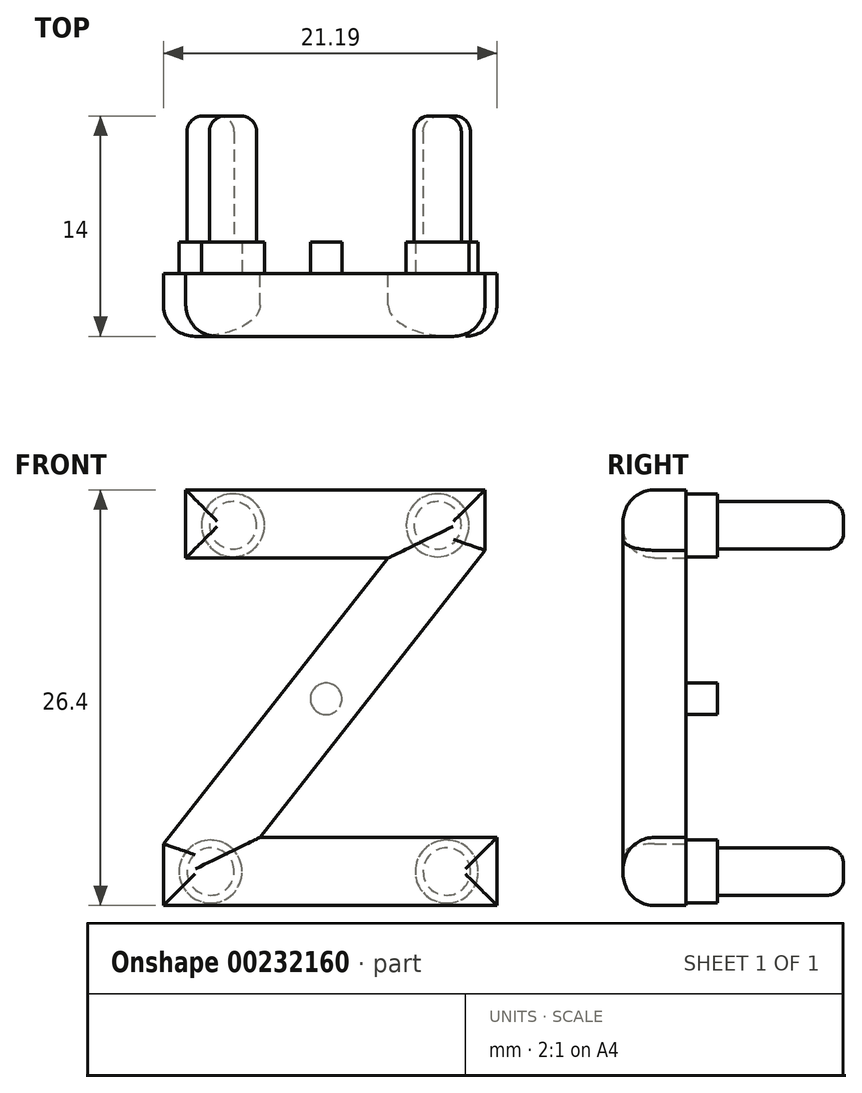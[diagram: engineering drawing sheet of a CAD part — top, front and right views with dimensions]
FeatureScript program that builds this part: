
annotation { "Feature Type Name" : "Feature", "Feature Type Description" : "" }
export const myFeature = defineFeature(function(context is Context, id is Id, definition is map)
    precondition{}
    {
        {
            var Q0;
            Q0=qCreatedBy(makeId("Front.planeOp"),FACE);
            var sketch = newSketch(context, id + "F0", { "sketchPlane" : qUnion([Q0])});
            skText(sketch, "E0", { "text": "Z", "fontName": "Arimo-Bold.ttf"});
            const initialGuessF0  = {"E0": [-0.01481, -0.01752, 1, 0, 0.02763]};
            skSetInitialGuess(sketch, initialGuessF0);
            skSolve(sketch);
        }
        {
            var Q0;
            Q0 = qSketchRegion(id + "F0", true);
            extrude(context, id + "F1", {"entities" : qUnion([Q0]), "depth" : 4 * mm});
        }
        {
            var Q0;
            Q0=makeQuery(id+"F1.opExtrude","CAP_EDGE",EDGE,{"disambiguationData":[OSD([sQuery(id+"F0.wireOp",EDGE,"E0.sketch_text.stroke-4")])],"isStart":false});
            var Q1;
            Q1=makeQuery(id+"F1.opExtrude","CAP_EDGE",EDGE,{"disambiguationData":[OSD([sQuery(id+"F0.wireOp",EDGE,"E0.sketch_text.stroke-5")])],"isStart":false});
            var Q2;
            Q2=makeQuery(id+"F1.opExtrude","CAP_EDGE",EDGE,{"disambiguationData":[OSD([sQuery(id+"F0.wireOp",EDGE,"E0.sketch_text.stroke-3")])],"isStart":false});
            var Q3;
            Q3=makeQuery(id+"F1.opExtrude","CAP_EDGE",EDGE,{"disambiguationData":[OSD([sQuery(id+"F0.wireOp",EDGE,"E0.sketch_text.stroke-6")])],"isStart":false});
            var Q4;
            Q4=makeQuery(id+"F1.opExtrude","CAP_EDGE",EDGE,{"disambiguationData":[OSD([sQuery(id+"F0.wireOp",EDGE,"E0.sketch_text.stroke-7")])],"isStart":false});
            var Q5;
            Q5=makeQuery(id+"F1.opExtrude","CAP_EDGE",EDGE,{"disambiguationData":[OSD([sQuery(id+"F0.wireOp",EDGE,"E0.sketch_text.stroke-2")])],"isStart":false});
            var Q6;
            Q6=makeQuery(id+"F1.opExtrude","CAP_EDGE",EDGE,{"disambiguationData":[OSD([sQuery(id+"F0.wireOp",EDGE,"E0.sketch_text.stroke-1")])],"isStart":false});
            var Q7;
            Q7=makeQuery(id+"F1.opExtrude","CAP_EDGE",EDGE,{"disambiguationData":[OSD([sQuery(id+"F0.wireOp",EDGE,"E0.sketch_text.stroke-8")])],"isStart":false});
            var Q8;
            Q8=makeQuery(id+"F1.opExtrude","CAP_EDGE",EDGE,{"disambiguationData":[OSD([sQuery(id+"F0.wireOp",EDGE,"E0.sketch_text.stroke-0")])],"isStart":false});
            var Q9;
            Q9=makeQuery(id+"F1.opExtrude","CAP_EDGE",EDGE,{"disambiguationData":[OSD([sQuery(id+"F0.wireOp",EDGE,"E0.sketch_text.stroke-9")])],"isStart":false});
            fillet(context, id + "F2", {"entities" : qUnion([Q0, Q1, Q2, Q3, Q4, Q5, Q6, Q7, Q8, Q9]), "radius" : 2 * mm, "tangentPropagation" : true, "allowEdgeOverflow" : false});
        }
        {
            var Q0;
            Q0=makeQuery(id+"F1.opExtrude","CAP_FACE",FACE,{"disambiguationData":[OSD([sQuery(id+"F0.wireOp",EDGE,"E0.sketch_text.stroke-0"),sQuery(id+"F0.wireOp",EDGE,"E0.sketch_text.stroke-1"),sQuery(id+"F0.wireOp",EDGE,"E0.sketch_text.stroke-2"),sQuery(id+"F0.wireOp",EDGE,"E0.sketch_text.stroke-3"),sQuery(id+"F0.wireOp",EDGE,"E0.sketch_text.stroke-4"),sQuery(id+"F0.wireOp",EDGE,"E0.sketch_text.stroke-5"),sQuery(id+"F0.wireOp",EDGE,"E0.sketch_text.stroke-6"),sQuery(id+"F0.wireOp",EDGE,"E0.sketch_text.stroke-7"),sQuery(id+"F0.wireOp",EDGE,"E0.sketch_text.stroke-8"),sQuery(id+"F0.wireOp",EDGE,"E0.sketch_text.stroke-9")])],"isStart":true});
            var sketch = newSketch(context, id + "F3", { "sketchPlane" : qUnion([Q0])});
            skCircle(sketch, "E1", {"center": v(-3.75, 6.63) * mm, "radius": 1.5 * mm});
            skPoint(sketch, "E1.centerSnap0", {"position": v(-8.6, 6.63) * mm});
            skCircle(sketch, "E2", {"center": v(9.25, 6.63) * mm, "radius": 1.5 * mm});
            skCircle(sketch, "E3", {"center": v(10.67, -15.37) * mm, "radius": 1.5 * mm});
            skCircle(sketch, "E4", {"center": v(-4.33, -15.37) * mm, "radius": 1.5 * mm});
            skSolve(sketch);
        }
        {
            var Q0;
            Q0=makeQuery(id+"F3.imprint","IMPRINT",FACE,{"disambiguationData":[TD([[makeQuery(id+"F3.imprint","IMPRINT",EDGE,{"derivedFrom":sQuery(id+"F3.wireOp",EDGE,"E2")}),1.0]])]});
            var Q1;
            Q1=makeQuery(id+"F3.imprint","IMPRINT",FACE,{"disambiguationData":[TD([[makeQuery(id+"F3.imprint","IMPRINT",EDGE,{"derivedFrom":sQuery(id+"F3.wireOp",EDGE,"E1")}),1.0]])]});
            var Q2;
            Q2=makeQuery(id+"F3.imprint","IMPRINT",FACE,{"disambiguationData":[TD([[makeQuery(id+"F3.imprint","IMPRINT",EDGE,{"derivedFrom":sQuery(id+"F3.wireOp",EDGE,"vsQ1oQda-6UFy-wekB-KQ1m-gjQAgTjeKQk8")}),1.0]])]});
            var Q3;
            Q3=makeQuery(id+"F3.imprint","IMPRINT",FACE,{"disambiguationData":[TD([[makeQuery(id+"F3.imprint","IMPRINT",EDGE,{"derivedFrom":sQuery(id+"F3.wireOp",EDGE,"E4")}),1.0]])]});
            var Q4;
            Q4=makeQuery(id+"F3.imprint","IMPRINT",FACE,{"disambiguationData":[TD([[makeQuery(id+"F3.imprint","IMPRINT",EDGE,{"derivedFrom":sQuery(id+"F3.wireOp",EDGE,"E3")}),1.0]])]});
            extrude(context, id + "F4", {"entities" : qUnion([Q0, Q1, Q2, Q3, Q4]), "operationType" : NewBodyOperationType.ADD, "depth" : 10 * mm});
        }
        {
            var Q0;
            Q0=makeQuery(id+"F1.opExtrude","CAP_FACE",FACE,{"disambiguationData":[OSD([sQuery(id+"F0.wireOp",EDGE,"E0.sketch_text.stroke-0"),sQuery(id+"F0.wireOp",EDGE,"E0.sketch_text.stroke-1"),sQuery(id+"F0.wireOp",EDGE,"E0.sketch_text.stroke-2"),sQuery(id+"F0.wireOp",EDGE,"E0.sketch_text.stroke-3"),sQuery(id+"F0.wireOp",EDGE,"E0.sketch_text.stroke-4"),sQuery(id+"F0.wireOp",EDGE,"E0.sketch_text.stroke-5"),sQuery(id+"F0.wireOp",EDGE,"E0.sketch_text.stroke-6"),sQuery(id+"F0.wireOp",EDGE,"E0.sketch_text.stroke-7"),sQuery(id+"F0.wireOp",EDGE,"E0.sketch_text.stroke-8"),sQuery(id+"F0.wireOp",EDGE,"E0.sketch_text.stroke-9")])],"isStart":true});
            var sketch = newSketch(context, id + "F5", { "sketchPlane" : qUnion([Q0])});
            skCircle(sketch, "E5", {"center": v(3.33, -4.4) * mm, "radius": 1 * mm});
            skCircle(sketch, "E6", {"center": v(-3.75, 6.63) * mm, "radius": 2 * mm});
            skCircle(sketch, "E7", {"center": v(9.25, 6.63) * mm, "radius": 2 * mm});
            skCircle(sketch, "E8", {"center": v(-4.33, -15.37) * mm, "radius": 2 * mm});
            skCircle(sketch, "E9", {"center": v(10.67, -15.37) * mm, "radius": 2 * mm});
            skSolve(sketch);
        }
        {
            var Q0;
            Q0 = qSketchRegion(id + "F5", true);
            extrude(context, id + "F6", {"entities" : qUnion([Q0]), "operationType" : NewBodyOperationType.ADD, "depth" : 2 * mm});
        }
        {
            var Q0;
            Q0=makeQuery(id+"F4.opExtrude","CAP_EDGE",EDGE,{"disambiguationData":[OSD([sQuery(id+"F3.wireOp",EDGE,"E1")])],"isStart":false});
            var Q1;
            Q1=makeQuery(id+"F4.opExtrude","CAP_EDGE",EDGE,{"disambiguationData":[OSD([sQuery(id+"F3.wireOp",EDGE,"E2")])],"isStart":false});
            var Q2;
            Q2=makeQuery(id+"F4.opExtrude","CAP_EDGE",EDGE,{"disambiguationData":[OSD([sQuery(id+"F3.wireOp",EDGE,"vsQ1oQda-6UFy-wekB-KQ1m-gjQAgTjeKQk8")])],"isStart":false});
            var Q3;
            Q3=makeQuery(id+"F4.opExtrude","CAP_EDGE",EDGE,{"disambiguationData":[OSD([sQuery(id+"F3.wireOp",EDGE,"E4")])],"isStart":false});
            var Q4;
            Q4=makeQuery(id+"F4.opExtrude","CAP_EDGE",EDGE,{"disambiguationData":[OSD([sQuery(id+"F3.wireOp",EDGE,"E3")])],"isStart":false});
            fillet(context, id + "F7", {"entities" : qUnion([Q0, Q1, Q2, Q3, Q4]), "radius" : 1 * mm, "tangentPropagation" : true, "allowEdgeOverflow" : false});
        }
    });
